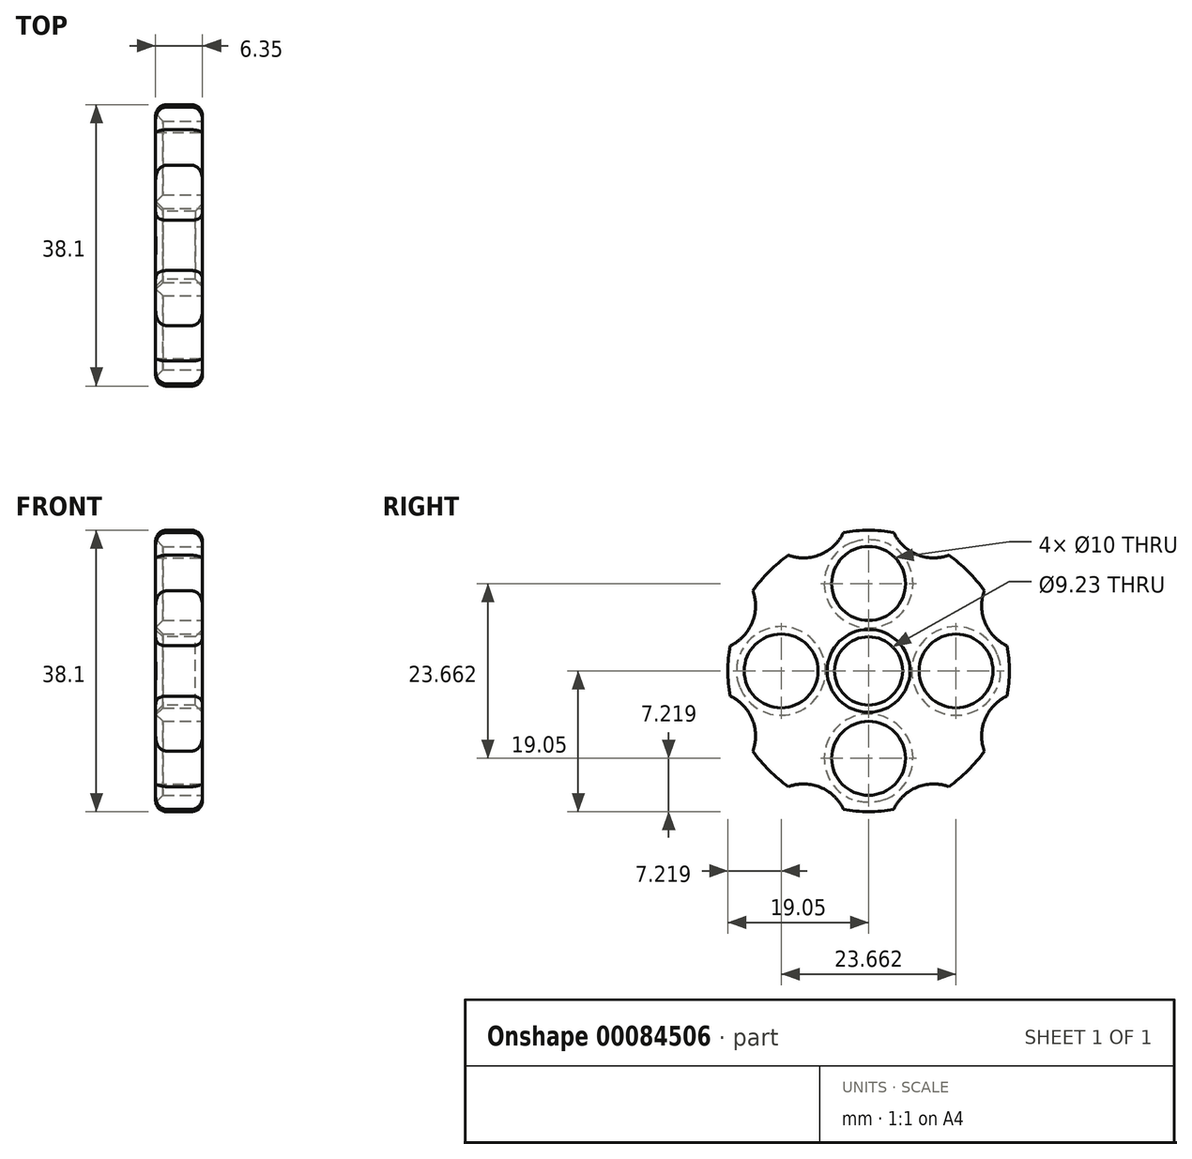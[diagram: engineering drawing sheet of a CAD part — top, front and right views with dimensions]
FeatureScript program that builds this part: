
annotation { "Feature Type Name" : "Feature", "Feature Type Description" : "" }
export const myFeature = defineFeature(function(context is Context, id is Id, definition is map)
    precondition{}
    {
        {
            var Q0;
            Q0=qCreatedBy(makeId("Right.planeOp"),FACE);
            var sketch = newSketch(context, id + "F0", { "sketchPlane" : qUnion([Q0])});
            skCircle(sketch, "E0", {"center": v(0, 0) * mm, "radius": 4.61 * mm});
            skCircle(sketch, "E1", {"center": v(0, 0) * mm, "radius": 19.05 * mm});
            skSolve(sketch);
        }
        {
            var Q0;
            Q0 = qSketchRegion(id + "F0", true);
            extrude(context, id + "F1", {"entities" : qUnion([Q0]), "depth" : 6.35 * mm});
        }
        {
            var Q0;
            Q0=makeQuery(id+"F1.opExtrude","CAP_FACE",FACE,{"disambiguationData":[OSD([sQuery(id+"F0.wireOp",EDGE,"E0"),sQuery(id+"F0.wireOp",EDGE,"E1")])],"isStart":false});
            var sketch = newSketch(context, id + "F2", { "sketchPlane" : qUnion([Q0])});
            skCircle(sketch, "E2", {"center": v(0, 11.83) * mm, "radius": 5 * mm});
            skLineSegment(sketch, "E3", {"start": v(0, 19.05) * mm, "end": v(0, 4.61) * mm, "construction": true});
            skCircle(sketch, "E4.1.0", {"center": v(-11.83, 0) * mm, "radius": 5 * mm});
            skCircle(sketch, "E4.2.0", {"center": v(0, -11.83) * mm, "radius": 5 * mm});
            skPoint(sketch, "E4.center", {"position": v(0, 0) * mm});
            skCircle(sketch, "E5.1.3.0", {"center": v(11.83, 0) * mm, "radius": 5 * mm});
            skSolve(sketch);
        }
        {
            var Q0;
            Q0 = qSketchRegion(id + "F2", true);
            extrude(context, id + "F3", {"entities" : qUnion([Q0]), "operationType" : NewBodyOperationType.REMOVE, "endBound" : BoundingType.THROUGH_ALL, "oppositeDirection" : true, "depth" : 25 * mm});
        }
        {
            var Q0;
            Q0=makeQuery(id+"F3.boolean.opBoolean","COPY",EDGE,{"derivedFrom":makeQuery(id+"F3.opExtrude","CAP_EDGE",EDGE,{"disambiguationData":[OSD([sQuery(id+"F2.wireOp",EDGE,"E2")])],"isStart":true})});
            var Q1;
            Q1=makeQuery(id+"F3.boolean.opBoolean","INTERSECT",EDGE,{"derivedFrom":[makeQuery(id+"F1.opExtrude","CAP_FACE",FACE,{"disambiguationData":[OSD([sQuery(id+"F0.wireOp",EDGE,"E0"),sQuery(id+"F0.wireOp",EDGE,"E1")])],"isStart":true}),makeQuery(id+"F3.opExtrude","SWEPT_FACE",FACE,{"disambiguationData":[OSD([sQuery(id+"F2.wireOp",EDGE,"E2")])]})]});
            var Q2;
            Q2=makeQuery(id+"F1.opExtrude","CAP_EDGE",EDGE,{"disambiguationData":[OSD([sQuery(id+"F0.wireOp",EDGE,"E0")])],"isStart":false});
            var Q3;
            Q3=makeQuery(id+"F1.opExtrude","CAP_EDGE",EDGE,{"disambiguationData":[OSD([sQuery(id+"F0.wireOp",EDGE,"E0")])],"isStart":true});
            var Q4;
            Q4=makeQuery(id+"F3.boolean.opBoolean","COPY",EDGE,{"derivedFrom":makeQuery(id+"F3.opExtrude","CAP_EDGE",EDGE,{"disambiguationData":[OSD([sQuery(id+"F2.wireOp",EDGE,"E5.1.3.0")])],"isStart":true})});
            var Q5;
            Q5=makeQuery(id+"F3.boolean.opBoolean","INTERSECT",EDGE,{"derivedFrom":[makeQuery(id+"F1.opExtrude","CAP_FACE",FACE,{"disambiguationData":[OSD([sQuery(id+"F0.wireOp",EDGE,"E0"),sQuery(id+"F0.wireOp",EDGE,"E1")])],"isStart":true}),makeQuery(id+"F3.opExtrude","SWEPT_FACE",FACE,{"disambiguationData":[OSD([sQuery(id+"F2.wireOp",EDGE,"E5.1.3.0")])]})]});
            var Q6;
            Q6=makeQuery(id+"F3.boolean.opBoolean","INTERSECT",EDGE,{"derivedFrom":[makeQuery(id+"F1.opExtrude","CAP_FACE",FACE,{"disambiguationData":[OSD([sQuery(id+"F0.wireOp",EDGE,"E0"),sQuery(id+"F0.wireOp",EDGE,"E1")])],"isStart":true}),makeQuery(id+"F3.opExtrude","SWEPT_FACE",FACE,{"disambiguationData":[OSD([sQuery(id+"F2.wireOp",EDGE,"E4.1.0")])]})]});
            var Q7;
            Q7=makeQuery(id+"F3.boolean.opBoolean","COPY",EDGE,{"derivedFrom":makeQuery(id+"F3.opExtrude","CAP_EDGE",EDGE,{"disambiguationData":[OSD([sQuery(id+"F2.wireOp",EDGE,"E4.1.0")])],"isStart":true})});
            var Q8;
            Q8=makeQuery(id+"F3.boolean.opBoolean","INTERSECT",EDGE,{"derivedFrom":[makeQuery(id+"F1.opExtrude","CAP_FACE",FACE,{"disambiguationData":[OSD([sQuery(id+"F0.wireOp",EDGE,"E0"),sQuery(id+"F0.wireOp",EDGE,"E1")])],"isStart":true}),makeQuery(id+"F3.opExtrude","SWEPT_FACE",FACE,{"disambiguationData":[OSD([sQuery(id+"F2.wireOp",EDGE,"E4.2.0")])]})]});
            var Q9;
            Q9=makeQuery(id+"F3.boolean.opBoolean","COPY",EDGE,{"derivedFrom":makeQuery(id+"F3.opExtrude","CAP_EDGE",EDGE,{"disambiguationData":[OSD([sQuery(id+"F2.wireOp",EDGE,"E4.2.0")])],"isStart":true})});
            chamfer(context, id + "F4", {"entities" : qUnion([Q0, Q1, Q2, Q3, Q4, Q5, Q6, Q7, Q8, Q9]), "width" : 1 * mm, "tangentPropagation" : true});
        }
        {
            var Q0;
            Q0=makeQuery(id+"F1.opExtrude","CAP_EDGE",EDGE,{"disambiguationData":[OSD([sQuery(id+"F0.wireOp",EDGE,"E1")])],"isStart":false});
            var Q1;
            Q1=makeQuery(id+"F1.opExtrude","CAP_EDGE",EDGE,{"disambiguationData":[OSD([sQuery(id+"F0.wireOp",EDGE,"E1")])],"isStart":true});
            fillet(context, id + "F5", {"entities" : qUnion([Q0, Q1]), "radius" : 1.5 * mm, "tangentPropagation" : true, "allowEdgeOverflow" : false});
        }
        {
            var Q0;
            Q0=makeQuery(id+"F1.opExtrude","CAP_FACE",FACE,{"disambiguationData":[OSD([sQuery(id+"F0.wireOp",EDGE,"E0"),sQuery(id+"F0.wireOp",EDGE,"E1")])],"isStart":false});
            var sketch = newSketch(context, id + "F6", { "sketchPlane" : qUnion([Q0])});
            skLineSegment(sketch, "E6", {"start": v(0, 0) * mm, "end": v(10.38, 25.06) * mm, "construction": true});
            skCircle(sketch, "E7", {"center": v(8.8, 21.25) * mm, "radius": 5.95 * mm});
            skPoint(sketch, "E8", {"position": v(6.52, 15.75) * mm});
            skPoint(sketch, "E9", {"position": v(7.3, 17.6) * mm});
            skCircle(sketch, "E10.1.0", {"center": v(-8.8, 21.25) * mm, "radius": 5.95 * mm});
            skCircle(sketch, "E10.2.0", {"center": v(-21.25, 8.8) * mm, "radius": 5.95 * mm});
            skCircle(sketch, "E10.3.0", {"center": v(-21.25, -8.8) * mm, "radius": 5.95 * mm});
            skCircle(sketch, "E10.4.0", {"center": v(-8.8, -21.25) * mm, "radius": 5.95 * mm});
            skCircle(sketch, "E10.5.0", {"center": v(8.8, -21.25) * mm, "radius": 5.95 * mm});
            skCircle(sketch, "E10.6.0", {"center": v(21.25, -8.8) * mm, "radius": 5.95 * mm});
            skCircle(sketch, "E10.7.0", {"center": v(21.25, 8.8) * mm, "radius": 5.95 * mm});
            skPoint(sketch, "E10.center", {"position": v(0, 0) * mm});
            skSolve(sketch);
        }
        {
            var Q0;
            Q0 = qSketchRegion(id + "F6", true);
            extrude(context, id + "F7", {"entities" : qUnion([Q0]), "operationType" : NewBodyOperationType.REMOVE, "endBound" : BoundingType.THROUGH_ALL, "oppositeDirection" : true, "depth" : 25 * mm});
        }
    });
